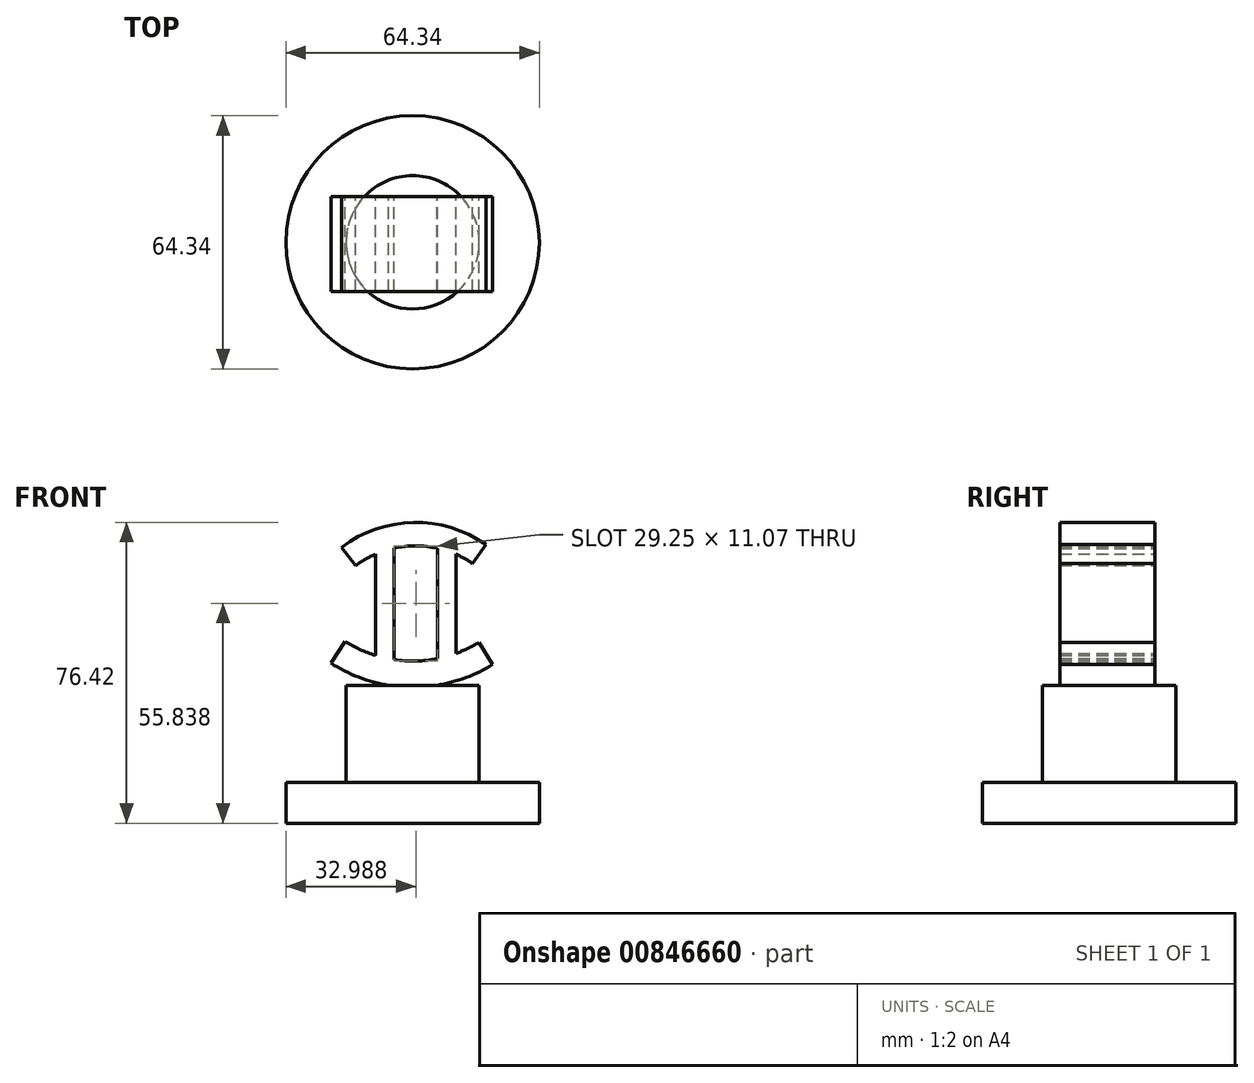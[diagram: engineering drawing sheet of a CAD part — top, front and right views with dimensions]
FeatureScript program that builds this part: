
annotation { "Feature Type Name" : "Feature", "Feature Type Description" : "" }
export const myFeature = defineFeature(function(context is Context, id is Id, definition is map)
    precondition{}
    {
        {
            var Q0;
            Q0=qCreatedBy(makeId("Front.planeOp"),FACE);
            var sketch = newSketch(context, id + "F0", { "sketchPlane" : qUnion([Q0])});
            skLineSegment(sketch, "E0", {"start": v(0, 0) * mm, "end": v(32.17, 0) * mm});
            skLineSegment(sketch, "E1", {"start": v(32.17, 0) * mm, "end": v(32.17, 10.4) * mm});
            skLineSegment(sketch, "E2", {"start": v(32.17, 10.4) * mm, "end": v(0, 10.4) * mm});
            skLineSegment(sketch, "E3", {"start": v(0, 10.4) * mm, "end": v(0, 0) * mm});
            skSolve(sketch);
        }
        {
            var Q0;
            Q0=makeQuery(id+"F0.imprint","IMPRINT",FACE,{"disambiguationData":[TD([[makeQuery(id+"F0.imprint","IMPRINT",EDGE,{"derivedFrom":sQuery(id+"F0.wireOp",EDGE,"E0")}),1.0]])]});
            var Q1;
            Q1=sQuery(id+"F0.wireOp",EDGE,"E3");
            revolve(context, id + "F1", {"surfaceOperationType" : NewSurfaceOperationType.NEW, "entities" : qUnion([Q0]), "axis" : qUnion([Q1]), "revolveType" : RevolveType.FULL});
        }
        {
            var Q0;
            Q0=qCreatedBy(makeId("Top.planeOp"),FACE);
            var sketch = newSketch(context, id + "F2", { "sketchPlane" : qUnion([Q0])});
            skCircle(sketch, "E4", {"center": v(0, 0) * mm, "radius": 16.92 * mm});
            skSolve(sketch);
        }
        {
            var Q0;
            Q0 = qSketchRegion(id + "F2", true);
            extrude(context, id + "F3", {"entities" : qUnion([Q0]), "operationType" : NewBodyOperationType.ADD, "depth" : 35.05 * mm, "offsetDistance" : 25.4 * mm});
        }
        {
            var Q0;
            Q0=qCreatedBy(makeId("Front.planeOp"),FACE);
            var sketch = newSketch(context, id + "F4", { "sketchPlane" : qUnion([Q0])});
            skArc(sketch, "E5", {"start": v(-20.78, 40.67) * mm, "mid": v(-0.3, 34.55) * mm, "end": v(20.3, 40.32) * mm});
            skArc(sketch, "E6.0", {"start": v(-17.2, 46.22) * mm, "mid": v(-0.24, 41.16) * mm, "end": v(16.82, 45.94) * mm});
            skArc(sketch, "E7", {"start": v(-17.2, 46.22) * mm, "mid": v(-0.24, 41.2) * mm, "end": v(16.82, 45.94) * mm});
            skLineSegment(sketch, "E8", {"start": v(-17.2, 46.22) * mm, "end": v(-20.78, 40.67) * mm});
            skLineSegment(sketch, "E9", {"start": v(16.82, 45.94) * mm, "end": v(20.3, 40.32) * mm});
            skArc(sketch, "E10", {"start": v(18.6, 70.78) * mm, "mid": v(0.17, 76.42) * mm, "end": v(-18.03, 70.1) * mm});
            skArc(sketch, "E11.0", {"start": v(15.24, 66) * mm, "mid": v(0.28, 70.58) * mm, "end": v(-14.5, 65.45) * mm});
            skArc(sketch, "E12", {"start": v(15.24, 66) * mm, "mid": v(0.28, 70.46) * mm, "end": v(-14.5, 65.45) * mm});
            skLineSegment(sketch, "E13", {"start": v(-18.03, 70.1) * mm, "end": v(-14.5, 65.45) * mm});
            skLineSegment(sketch, "E14", {"start": v(18.6, 70.78) * mm, "end": v(15.24, 66) * mm});
            skLineSegment(sketch, "E15", {"start": v(-9.45, 68.35) * mm, "end": v(-9.45, 42.64) * mm});
            skLineSegment(sketch, "E16", {"start": v(-4.72, 69.87) * mm, "end": v(-4.72, 41.56) * mm});
            skLineSegment(sketch, "E17", {"start": v(10.96, 68.35) * mm, "end": v(10.96, 43.12) * mm});
            skLineSegment(sketch, "E18", {"start": v(6.35, 69.85) * mm, "end": v(6.35, 41.83) * mm});
            skSolve(sketch);
        }
        {
            var Q0;
            Q0 = qSketchRegion(id + "F4", true);
            extrude(context, id + "F5", {"entities" : qUnion([Q0]), "operationType" : NewBodyOperationType.ADD, "depth" : 12.45 * mm, "offsetDistance" : 25.4 * mm});
        }
        {
            var Q0;
            Q0=makeQuery(id+"F5.opExtrude","CAP_FACE",FACE,{"disambiguationData":[OSD([sQuery(id+"F4.wireOp",EDGE,"E5"),sQuery(id+"F4.wireOp",EDGE,"E7"),sQuery(id+"F4.wireOp",EDGE,"E8"),sQuery(id+"F4.wireOp",EDGE,"E9"),sQuery(id+"F4.wireOp",EDGE,"E10"),sQuery(id+"F4.wireOp",EDGE,"E12"),sQuery(id+"F4.wireOp",EDGE,"E13"),sQuery(id+"F4.wireOp",EDGE,"E14"),sQuery(id+"F4.wireOp",EDGE,"E15"),sQuery(id+"F4.wireOp",EDGE,"E16"),sQuery(id+"F4.wireOp",EDGE,"E17"),sQuery(id+"F4.wireOp",EDGE,"E18")])],"isStart":true});
            extrude(context, id + "F6", {"entities" : qUnion([Q0]), "operationType" : NewBodyOperationType.ADD, "depth" : 11.68 * mm, "offsetDistance" : 25.4 * mm});
        }
    });
